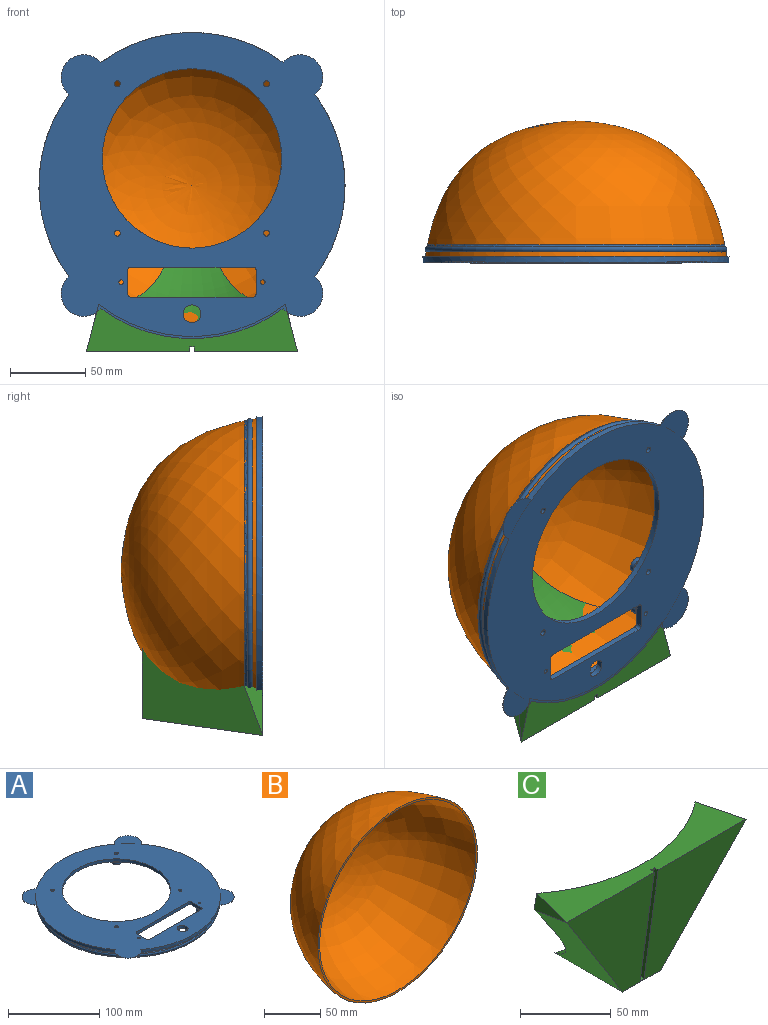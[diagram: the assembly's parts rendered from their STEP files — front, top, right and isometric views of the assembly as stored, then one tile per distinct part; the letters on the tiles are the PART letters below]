
ASSEMBLY  parts=3 mates=2
PART A: 61 faces, bbox 218.2x218.2x13.8 mm
  f0: cylinder r=101.5mm len=203mm, axis (0,0,-1), area 2502.9mm2, adj f2,f4,f53,f54,f55,f56,f57,f58
  f1: cylinder r=98.6mm len=197.2mm, axis (0,0,1), area 18.5mm2, adj f7,f28
  f2: plane 203x203mm, normal (0,0,1), area 20834.4mm2, adj f0,f8,f9,f10,f11,f12,f13,f23
  f3: plane 184x184mm, normal (0,0,-1), area 12196.7mm2, adj f8,f9,f10,f11,f14,f19,f21,f23
  f4: plane 203x203mm, normal (0,0,-1), area 1823mm2, adj f0,f6
  f5: cylinder r=95mm len=190mm, axis (0,0,1), area 2984.5mm2, adj f7,f14
  f6: cylinder r=98.6mm len=197.2mm, axis (0,0,1), area 1009.7mm2, adj f4,f29
  f7: plane 197.2x197.2mm, normal (0,0,-1), area 2189.6mm2, adj f1,f5
  f8: plane 81x4mm, normal (0,1,0), area 324mm2, adj f2,f3,f23,f26
  f9: plane 16.41x4.41mm, normal (-1,0,0), area 64mm2, adj f2,f3,f20,f25,f26
  f10: plane 81x4mm, normal (0,-1,0), area 324mm2, adj f2,f3,f24,f25
  f11: plane 16.41x4.41mm, normal (1,0,0), area 64mm2, adj f2,f3,f22,f23,f24
  f12: cylinder r=1.5mm len=10mm, axis (0,0,1), area 94.2mm2, adj f2,f16
  f13: cylinder r=1.5mm len=10mm, axis (0,0,1), area 94.2mm2, adj f2,f18
  f14: torus R=92mm, axis (0,0,1), area 2780.6mm2, adj f3,f5,f48,f50
  f15: cylinder r=3.5mm len=7mm, axis (0,0,1), area 68.2mm2, adj f16,f21,f22
  f16: plane 7x7mm, normal (0,0,-1), area 31.4mm2, adj f12,f15
  f17: cylinder r=3.5mm len=7mm, axis (0,0,1), area 68.2mm2, adj f18,f19,f20
  f18: plane 7x7mm, normal (0,0,-1), area 31.4mm2, adj f13,f17
  f19: torus R=6.5mm, axis (0,0,1), area 101mm2, adj f3,f17,f20
  f20: bspline ~9.95x3.23mm, area 21.6mm2, adj f9,f17,f19
  f21: torus R=6.5mm, axis (0,0,1), area 101mm2, adj f3,f15,f22
  f22: bspline ~9.95x3.23mm, area 21.6mm2, adj f11,f15,f21
  f23: cylinder r=2mm len=4mm, axis (0,0,-1), area 12.6mm2, adj f2,f3,f8,f11
  f24: cylinder r=2mm len=4mm, axis (0,0,1), area 12.6mm2, adj f2,f3,f10,f11
  f25: cylinder r=2mm len=4mm, axis (0,0,-1), area 12.6mm2, adj f2,f3,f9,f10
  f26: cylinder r=2mm len=4mm, axis (0,0,1), area 12.6mm2, adj f2,f3,f8,f9
  f27: torus R=98mm, axis (0,0,-1), area 2328.7mm2, adj f28,f29
  f28: torus R=100.6mm, axis (0,0,-1), area 1098mm2, adj f1,f27
  f29: torus R=100.6mm, axis (0,0,1), area 1098mm2, adj f6,f27
  f30: cylinder r=5.9mm len=10.8mm, axis (0,0,-1), area 54.6mm2, adj f2,f3,f31,f33
  f31: plane 4.75x4mm, normal (-1,0,0), area 19mm2, adj f2,f3,f30,f32
  f32: cylinder r=5.9mm len=10.8mm, axis (0,0,-1), area 54.6mm2, adj f2,f3,f31,f33
  f33: plane 4.75x4mm, normal (1,0,0), area 19mm2, adj f2,f3,f30,f32
  f34: cylinder r=59.5mm len=119mm, axis (0,0,-1), area 1495.4mm2, adj f2,f3
  f35: cylinder r=2mm len=12mm, axis (0,0,-1), area 150.8mm2, adj f2,f42
  f36: cylinder r=2mm len=12mm, axis (0,0,-1), area 150.8mm2, adj f2,f40
  f37: cylinder r=2mm len=12mm, axis (0,0,-1), area 150.8mm2, adj f2,f46
  f38: cylinder r=2mm len=12mm, axis (0,0,-1), area 150.8mm2, adj f2,f44
  f39: cylinder r=5mm len=10mm, axis (0,0,1), area 94.2mm2, adj f40,f52
  f40: plane 10x10mm, normal (0,0,-1), area 66mm2, adj f36,f39
  f41: cylinder r=5mm len=10mm, axis (0,0,1), area 94.2mm2, adj f42,f51
  f42: plane 10x10mm, normal (0,0,-1), area 66mm2, adj f35,f41
  f43: cylinder r=5mm len=10mm, axis (0,0,1), area 94.2mm2, adj f44,f49,f50
  f44: plane 10x10mm, normal (0,0,-1), area 66mm2, adj f38,f43
  f45: cylinder r=5mm len=10mm, axis (0,0,1), area 94.2mm2, adj f46,f47,f48
  f46: plane 10x10mm, normal (0,0,-1), area 66mm2, adj f37,f45
  f47: torus R=10mm, axis (0,0,1), area 269.5mm2, adj f3,f45,f48
  f48: bspline ~10.38x9.08mm, area 53.3mm2, adj f14,f45,f47
  f49: torus R=10mm, axis (0,0,1), area 269.5mm2, adj f3,f43,f50
  f50: bspline ~10.34x9.11mm, area 53.3mm2, adj f14,f43,f49
  f51: torus R=10mm, axis (0,0,1), area 336.4mm2, adj f3,f41
  f52: torus R=10mm, axis (0,0,1), area 336.4mm2, adj f3,f39
  f53: cylinder r=15mm len=26.36mm, axis (0,0,1), area 19.7mm2, adj f0,f2,f54
  f54: plane 26.36x26.36mm, normal (0,0,-1), area 364.5mm2, adj f0,f53
  f55: cylinder r=15mm len=26.36mm, axis (0,0,1), area 19.7mm2, adj f0,f2,f56
  f56: plane 26.36x26.36mm, normal (0,0,-1), area 364.5mm2, adj f0,f55
  f57: cylinder r=15mm len=26.36mm, axis (0,0,1), area 19.7mm2, adj f0,f2,f58
  f58: plane 26.36x26.36mm, normal (0,0,-1), area 364.5mm2, adj f0,f57
  f59: cylinder r=15mm len=26.36mm, axis (0,0,1), area 19.7mm2, adj f0,f2,f60
  f60: plane 26.36x26.36mm, normal (0,0,-1), area 364.5mm2, adj f0,f59
PART B: 3 faces, bbox 200x90x200 mm
  f0: revolved ~200x200mm, area 58047.9mm2, adj f1
  f1: plane 200x200mm, normal (0,-1,0), area 1256.7mm2, adj f0,f2
  f2: revolved ~195.96x195.96mm, area 55653.5mm2, adj f1
PART C: 12 faces, bbox 140.2x72.7x80.2 mm
  f0: plane 140x31.42mm, normal (0,0,1), area 2325.4mm2, adj f1,f5,f6,f7,f8,f10,f11
  f1: plane 140x80mm, normal (0,-0.99,-0.14), area 6626.8mm2, adj f0,f2,f3,f4,f8,f9,f10
  f2: plane 52.87x30mm, normal (0,0,-1), area 1538mm2, adj f1,f3,f4,f7
  f3: plane 80x64.11mm, normal (0.82,0,-0.57), area 2944.6mm2, adj f1,f2,f6,f7
  f4: plane 80x64.11mm, normal (-0.82,0,-0.57), area 2944.6mm2, adj f1,f2,f5,f7
  f5: plane 34.65x13.22mm, normal (-0.97,0.25,0), area 209.7mm2, adj f0,f4,f7
  f6: plane 34.64x13.22mm, normal (0.97,0.25,0), area 209.7mm2, adj f0,f3,f7
  f7: revolved ~125.69x80mm, area 8119.6mm2, adj f0,f2,f3,f4,f5,f6
  f8: plane 79.22x14.1mm, normal (1,0,0), area 239.4mm2, adj f0,f1,f9,f11
  f9: plane 3x2.97mm, normal (0,-0.14,0.99), area 9mm2, adj f1,f8,f10,f11
  f10: plane 79.22x14.1mm, normal (-1,0,0), area 239.4mm2, adj f0,f1,f9,f11
  f11: plane 78.8x11.08mm, normal (0,-0.99,-0.14), area 238.7mm2, adj f0,f8,f9,f10
PLACE A rot(axis=(1,0,0),90deg) t=(-8.3,-39.46,33.67)mm
PLACE B t=(-8.3,50.54,33.67)mm
PLACE C rot(axis=(1,0,0),90deg) t=(-8.3,46.54,33.67)mm
MATE fastened C.f0 <-> A.f0  axis (0,-1,0) through (-8.3,-43.46,33.67)mm
MATE fastened A.f0 <-> B.f1  axis (0,1,0) through (-8.3,-39.46,33.67)mm
